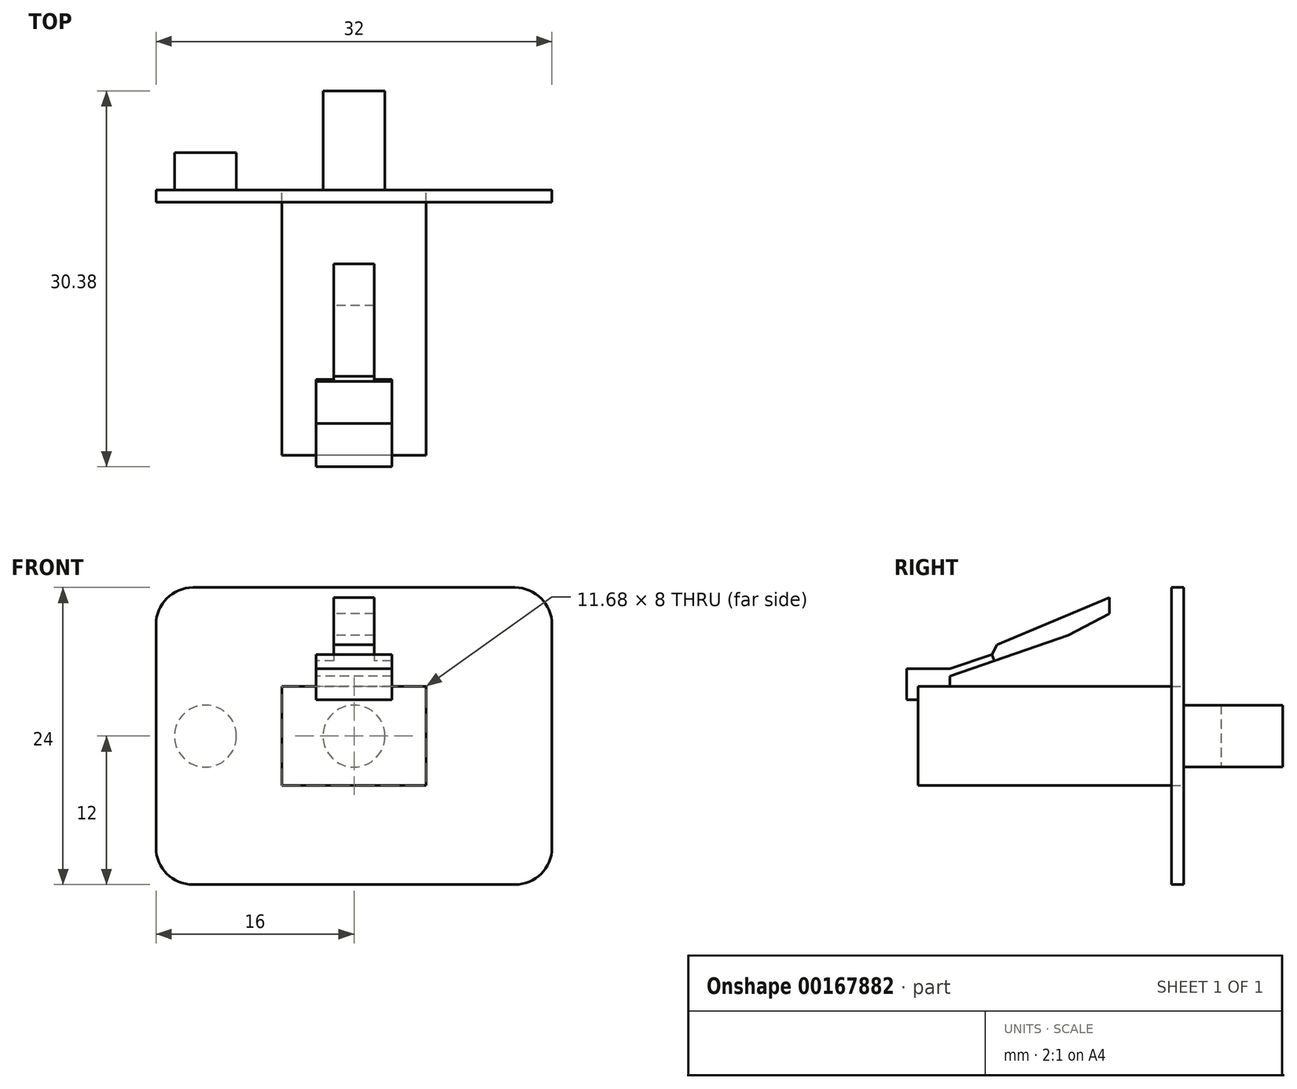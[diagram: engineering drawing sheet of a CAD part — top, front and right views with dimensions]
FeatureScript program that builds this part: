
annotation { "Feature Type Name" : "Feature", "Feature Type Description" : "" }
export const myFeature = defineFeature(function(context is Context, id is Id, definition is map)
    precondition{}
    {
        {
            var Q0;
            Q0=qCreatedBy(makeId("Right.planeOp"),FACE);
            var sketch = newSketch(context, id + "F0", { "sketchPlane" : qUnion([Q0])});
            skLineSegment(sketch, "E0.bottom", {"start": v(0, 0) * mm, "end": v(21.45, 0) * mm});
            skLineSegment(sketch, "E0.top", {"start": v(0, -8) * mm, "end": v(21.45, -8) * mm});
            skLineSegment(sketch, "E0.left", {"start": v(0, 0) * mm, "end": v(0, -8) * mm});
            skLineSegment(sketch, "E0.right", {"start": v(21.45, 0) * mm, "end": v(21.45, -8) * mm});
            skSolve(sketch);
        }
        {
            var Q0;
            Q0 = qSketchRegion(id + "F0", true);
            extrude(context, id + "F1", {"entities" : qUnion([Q0]), "depth" : 11.68 * mm / 2, "hasSecondDirection" : true, "secondDirectionOppositeDirection" : true, "secondDirectionDepth" : 11.68 * mm / 2});
        }
        {
            var Q0;
            Q0=qCreatedBy(makeId("Right.planeOp"),FACE);
            var sketch = newSketch(context, id + "F2", { "sketchPlane" : qUnion([Q0])});
            skLineSegment(sketch, "E1", {"start": v(0, -1.07) * mm, "end": v(-0.93, -1.07) * mm});
            skLineSegment(sketch, "E2", {"start": v(-0.93, -1.07) * mm, "end": v(-0.93, 1.43) * mm});
            skLineSegment(sketch, "E3", {"start": v(-0.93, 1.43) * mm, "end": v(2.57, 1.43) * mm});
            skLineSegment(sketch, "E4", {"start": v(2.57, 1.43) * mm, "end": v(5.96, 2.6) * mm});
            skLineSegment(sketch, "E5", {"start": v(5.96, 2.6) * mm, "end": v(6.38, 3.38) * mm});
            skLineSegment(sketch, "E6", {"start": v(6.38, 3.38) * mm, "end": v(15.45, 7.2) * mm});
            skLineSegment(sketch, "E7", {"start": v(15.45, 7.2) * mm, "end": v(15.45, 5.9) * mm});
            skLineSegment(sketch, "E8", {"start": v(15.45, 5.9) * mm, "end": v(12.1, 4.13) * mm});
            skLineSegment(sketch, "E9", {"start": v(12.1, 4.13) * mm, "end": v(2.57, 0.83) * mm});
            skLineSegment(sketch, "E10", {"start": v(2.57, 0.83) * mm, "end": v(2.57, 0) * mm});
            skLineSegment(sketch, "E11", {"start": v(5.96, 2.6) * mm, "end": v(6.15, 2.06) * mm});
            skLineSegment(sketch, "E12", {"start": v(0, -1.07) * mm, "end": v(0, 0) * mm});
            skLineSegment(sketch, "E13", {"start": v(0, 0) * mm, "end": v(2.57, 0) * mm});
            skSolve(sketch);
        }
        {
            var Q0;
            Q0=makeQuery(id+"F2.imprint","IMPRINT",FACE,{"disambiguationData":[TD([[makeQuery(id+"F2.imprint","IMPRINT",EDGE,{"derivedFrom":sQuery(id+"F2.wireOp",EDGE,"E1")}),-1.0]])]});
            extrude(context, id + "F3", {"entities" : qUnion([Q0]), "operationType" : NewBodyOperationType.ADD, "depth" : 3.05 * mm, "hasSecondDirection" : true, "secondDirectionOppositeDirection" : true, "secondDirectionDepth" : 3.05 * mm});
        }
        {
            var Q0;
            Q0=makeQuery(id+"F2.imprint","IMPRINT",FACE,{"disambiguationData":[TD([[makeQuery(id+"F2.imprint","IMPRINT",EDGE,{"derivedFrom":sQuery(id+"F2.wireOp",EDGE,"E5")}),-1.0]])]});
            extrude(context, id + "F4", {"entities" : qUnion([Q0]), "operationType" : NewBodyOperationType.ADD, "depth" : 3.25 * mm / 2, "hasSecondDirection" : true, "secondDirectionOppositeDirection" : true, "secondDirectionDepth" : 3.25 * mm / 2});
        }
        {
            var Q0;
            Q0=qCreatedBy(makeId("Right.planeOp"),FACE);
            var sketch = newSketch(context, id + "F5", { "sketchPlane" : qUnion([Q0])});
            skLineSegment(sketch, "E14.0.0", {"start": v(6.38, 3.38) * mm, "end": v(5.96, 2.6) * mm, "construction": true});
            skLineSegment(sketch, "E14.0.1", {"start": v(5.96, 2.6) * mm, "end": v(6.15, 2.06) * mm, "construction": true});
            skLineSegment(sketch, "E14.0.2", {"start": v(6.15, 2.06) * mm, "end": v(12.1, 4.13) * mm, "construction": true});
            skLineSegment(sketch, "E14.0.3", {"start": v(12.1, 4.13) * mm, "end": v(15.45, 5.9) * mm, "construction": true});
            skLineSegment(sketch, "E14.0.4", {"start": v(15.45, 5.9) * mm, "end": v(15.45, 7.2) * mm, "construction": true});
            skLineSegment(sketch, "E14.0.5", {"start": v(15.45, 7.2) * mm, "end": v(6.38, 3.38) * mm, "construction": true});
            skLineSegment(sketch, "E14.1.0", {"start": v(21.45, 0) * mm, "end": v(0, 0) * mm, "construction": true});
            skLineSegment(sketch, "E14.1.1", {"start": v(0, 0) * mm, "end": v(0, -8) * mm, "construction": true});
            skLineSegment(sketch, "E14.1.2", {"start": v(0, -8) * mm, "end": v(21.45, -8) * mm, "construction": true});
            skLineSegment(sketch, "E14.1.3", {"start": v(21.45, -8) * mm, "end": v(21.45, 0) * mm, "construction": true});
            skLineSegment(sketch, "E15.bottom", {"start": v(24.45, 8) * mm, "end": v(20.45, 8) * mm});
            skLineSegment(sketch, "E15.top", {"start": v(24.45, -16) * mm, "end": v(20.45, -16) * mm});
            skLineSegment(sketch, "E15.left", {"start": v(24.45, 8) * mm, "end": v(24.45, -16) * mm});
            skLineSegment(sketch, "E15.right", {"start": v(20.45, 8) * mm, "end": v(20.45, -16) * mm});
            skSolve(sketch);
        }
        {
            var Q0;
            Q0=makeQuery(id+"F5.imprint","IMPRINT",FACE,{"disambiguationData":[TD([[makeQuery(id+"F5.imprint","IMPRINT",EDGE,{"derivedFrom":sQuery(id+"F5.wireOp",EDGE,"E15.bottom")}),1.0]])]});
            extrude(context, id + "F6", {"entities" : qUnion([Q0]), "depth" : 16 * mm, "hasSecondDirection" : true, "secondDirectionOppositeDirection" : true, "secondDirectionDepth" : 16 * mm});
        }
        {
            var Q0;
            Q0=makeQuery(id+"F1.opExtrude","SWEPT_BODY",BODY,{"disambiguationData":[OSD([sQuery(id+"F0.wireOp",EDGE,"E0.bottom"),sQuery(id+"F0.wireOp",EDGE,"E0.top"),sQuery(id+"F0.wireOp",EDGE,"E0.left"),sQuery(id+"F0.wireOp",EDGE,"E0.right")])]});
            var Q1;
            Q1=makeQuery(id+"F6.opExtrude","SWEPT_BODY",BODY,{"disambiguationData":[OSD([sQuery(id+"F5.wireOp",EDGE,"E15.bottom"),sQuery(id+"F5.wireOp",EDGE,"E15.top"),sQuery(id+"F5.wireOp",EDGE,"E15.left"),sQuery(id+"F5.wireOp",EDGE,"E15.right")])]});
            booleanBodies(context, id + "F7", {"operationType" : BooleanOperationType.SUBTRACTION, "tools" : qUnion([Q0]), "targets" : qUnion([Q1]), "keepTools" : true});
        }
        {
            var Q0;
            Q0=makeQuery(id+"F6.opExtrude","SWEPT_FACE",FACE,{"disambiguationData":[OSD([sQuery(id+"F5.wireOp",EDGE,"E15.left")])]});
            var sketch = newSketch(context, id + "F8", { "sketchPlane" : qUnion([Q0])});
            skCircle(sketch, "E16", {"center": v(-12, -4) * mm, "radius": 2.5 * mm});
            skCircle(sketch, "E17.MirrorC", {"center": v(12, -4) * mm, "radius": 2.5 * mm});
            skCircle(sketch, "E18", {"center": v(0, -4) * mm, "radius": 2.5 * mm});
            skSolve(sketch);
        }
        {
            var Q0;
            Q0=makeQuery(id+"F8.imprint","IMPRINT",FACE,{"disambiguationData":[TD([[makeQuery(id+"F8.imprint","IMPRINT",EDGE,{"derivedFrom":sQuery(id+"F8.wireOp",EDGE,"E16")}),1.0]])]});
            var Q1;
            Q1=makeQuery(id+"F8.imprint","IMPRINT",FACE,{"disambiguationData":[TD([[makeQuery(id+"F8.imprint","IMPRINT",EDGE,{"derivedFrom":sQuery(id+"F8.wireOp",EDGE,"E17.MirrorC")}),-1.0]])]});
            extrude(context, id + "F9", {"entities" : qUnion([Q0, Q1]), "operationType" : NewBodyOperationType.REMOVE, "oppositeDirection" : true, "depth" : 3 * mm});
        }
        {
            var Q0;
            Q0=makeQuery(id+"F8.imprint","IMPRINT",FACE,{"disambiguationData":[TD([[makeQuery(id+"F8.imprint","IMPRINT",EDGE,{"derivedFrom":sQuery(id+"F8.wireOp",EDGE,"E18")}),1.0]])]});
            extrude(context, id + "F10", {"entities" : qUnion([Q0]), "operationType" : NewBodyOperationType.ADD, "depth" : 5 * mm});
        }
        {
            var Q0;
            Q0=makeQuery(id+"F6.opExtrude","CAP_EDGE",EDGE,{"disambiguationData":[OSD([sQuery(id+"F5.wireOp",EDGE,"E15.bottom")])],"isStart":true});
            var Q1;
            Q1=makeQuery(id+"F6.opExtrude","CAP_EDGE",EDGE,{"disambiguationData":[OSD([sQuery(id+"F5.wireOp",EDGE,"E15.top")])],"isStart":true});
            var Q2;
            Q2=makeQuery(id+"F6.opExtrude","CAP_EDGE",EDGE,{"disambiguationData":[OSD([sQuery(id+"F5.wireOp",EDGE,"E15.top")])],"isStart":false});
            var Q3;
            Q3=makeQuery(id+"F6.opExtrude","CAP_EDGE",EDGE,{"disambiguationData":[OSD([sQuery(id+"F5.wireOp",EDGE,"E15.bottom")])],"isStart":false});
            fillet(context, id + "F11", {"entities" : qUnion([Q0, Q1, Q2, Q3]), "radius" : 3 * mm, "tangentPropagation" : true, "allowEdgeOverflow" : false});
        }
    });
